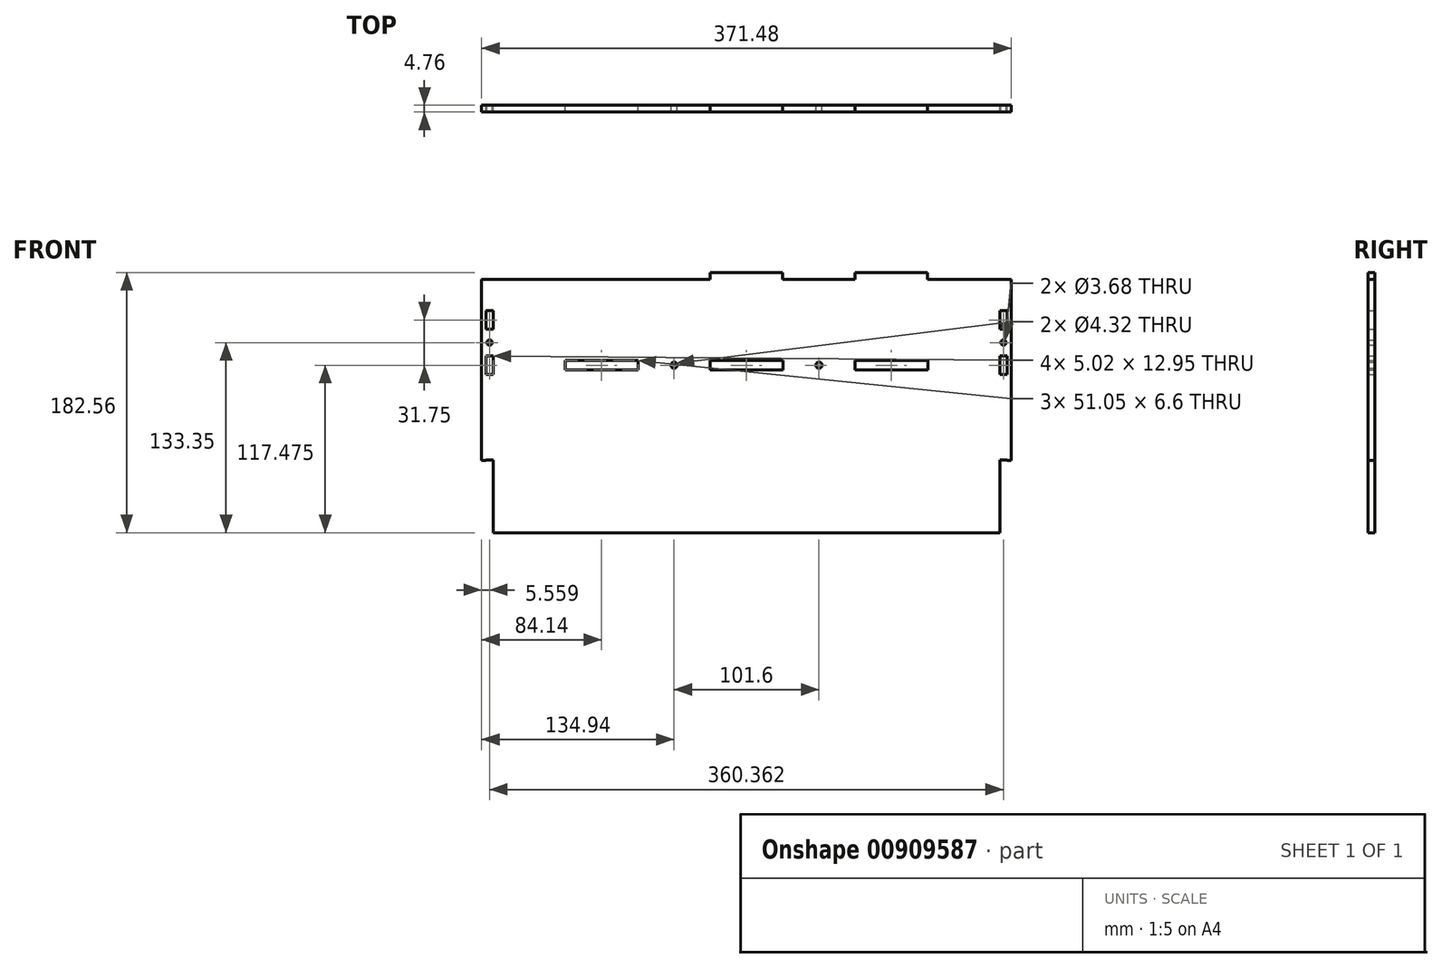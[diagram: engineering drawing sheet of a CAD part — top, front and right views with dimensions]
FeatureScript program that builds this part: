
annotation { "Feature Type Name" : "Feature", "Feature Type Description" : "" }
export const myFeature = defineFeature(function(context is Context, id is Id, definition is map)
    precondition{}
    {
        {
            var Q0;
            Q0=qCreatedBy(makeId("Front.planeOp"),FACE);
            var sketch = newSketch(context, id + "F0", { "sketchPlane" : qUnion([Q0])});
            skLineSegment(sketch, "E0.bottom", {"start": v(-182.56, 88.9) * mm, "end": v(182.56, 88.9) * mm});
            skLineSegment(sketch, "E0.top", {"start": v(-182.56, -88.9) * mm, "end": v(182.56, -88.9) * mm});
            skLineSegment(sketch, "E0.left", {"start": v(-182.56, 88.9) * mm, "end": v(-182.56, -88.9) * mm});
            skLineSegment(sketch, "E0.right", {"start": v(182.56, 88.9) * mm, "end": v(182.56, -88.9) * mm});
            skPoint(sketch, "E0.middle", {"position": v(0, 0) * mm});
            skLineSegment(sketch, "E1.0", {"start": v(-177.8, 88.9) * mm, "end": v(-177.8, -88.9) * mm, "construction": true});
            skLineSegment(sketch, "E2.0", {"start": v(177.8, 88.9) * mm, "end": v(177.8, -88.9) * mm, "construction": true});
            skLineSegment(sketch, "E3.bottom", {"start": v(-127, 31.75) * mm, "end": v(-76.2, 31.75) * mm});
            skLineSegment(sketch, "E3.top", {"start": v(-127, 25.4) * mm, "end": v(-76.2, 25.4) * mm});
            skLineSegment(sketch, "E3.left", {"start": v(-127, 31.75) * mm, "end": v(-127, 25.4) * mm});
            skLineSegment(sketch, "E3.right", {"start": v(-76.2, 31.75) * mm, "end": v(-76.2, 25.4) * mm});
            skLineSegment(sketch, "E4.0", {"start": v(-127.13, 31.88) * mm, "end": v(-76.07, 31.88) * mm});
            skLineSegment(sketch, "E4.1", {"start": v(-127.13, 31.88) * mm, "end": v(-127.13, 25.27) * mm});
            skLineSegment(sketch, "E4.2", {"start": v(-127.13, 25.27) * mm, "end": v(-76.07, 25.27) * mm});
            skLineSegment(sketch, "E4.3", {"start": v(-76.07, 31.88) * mm, "end": v(-76.07, 25.27) * mm});
            skLineSegment(sketch, "E5.1.0.0", {"start": v(-25.53, 31.88) * mm, "end": v(-25.53, 25.27) * mm});
            skLineSegment(sketch, "E5.1.0.1", {"start": v(-25.53, 31.88) * mm, "end": v(25.53, 31.88) * mm});
            skLineSegment(sketch, "E5.1.0.2", {"start": v(-25.53, 25.27) * mm, "end": v(25.53, 25.27) * mm});
            skLineSegment(sketch, "E5.1.0.3", {"start": v(25.4, 31.75) * mm, "end": v(25.4, 25.4) * mm});
            skLineSegment(sketch, "E5.1.0.4", {"start": v(-25.4, 31.75) * mm, "end": v(25.4, 31.75) * mm});
            skLineSegment(sketch, "E5.1.0.5", {"start": v(25.53, 31.88) * mm, "end": v(25.53, 25.27) * mm});
            skLineSegment(sketch, "E5.1.0.6", {"start": v(-25.4, 31.75) * mm, "end": v(-25.4, 25.4) * mm});
            skLineSegment(sketch, "E5.1.0.7", {"start": v(-25.4, 25.4) * mm, "end": v(25.4, 25.4) * mm});
            skLineSegment(sketch, "E5.2.0.0", {"start": v(76.07, 31.88) * mm, "end": v(76.07, 25.27) * mm});
            skLineSegment(sketch, "E5.2.0.1", {"start": v(76.07, 31.88) * mm, "end": v(127.13, 31.88) * mm});
            skLineSegment(sketch, "E5.2.0.2", {"start": v(76.07, 25.27) * mm, "end": v(127.13, 25.27) * mm});
            skLineSegment(sketch, "E5.2.0.3", {"start": v(127, 31.75) * mm, "end": v(127, 25.4) * mm});
            skLineSegment(sketch, "E5.2.0.4", {"start": v(76.2, 31.75) * mm, "end": v(127, 31.75) * mm});
            skLineSegment(sketch, "E5.2.0.5", {"start": v(127.13, 31.88) * mm, "end": v(127.13, 25.27) * mm});
            skLineSegment(sketch, "E5.2.0.6", {"start": v(76.2, 31.75) * mm, "end": v(76.2, 25.4) * mm});
            skLineSegment(sketch, "E5.2.0.7", {"start": v(76.2, 25.4) * mm, "end": v(127, 25.4) * mm});
            skLineSegment(sketch, "E5.direction1", {"start": v(-127, 25.4) * mm, "end": v(-25.4, 25.4) * mm, "construction": true});
            skLineSegment(sketch, "E6.bottom", {"start": v(-182.56, -88.9) * mm, "end": v(-177.8, -88.9) * mm});
            skLineSegment(sketch, "E6.top", {"start": v(-185.74, -38.1) * mm, "end": v(-177.8, -38.1) * mm});
            skLineSegment(sketch, "E6.left", {"start": v(-182.56, -88.9) * mm, "end": v(-182.56, -38.1) * mm});
            skLineSegment(sketch, "E6.right", {"start": v(-177.8, -88.9) * mm, "end": v(-177.8, -38.1) * mm});
            skLineSegment(sketch, "E7", {"start": v(0, 88.9) * mm, "end": v(0, -88.9) * mm, "construction": true});
            skLineSegment(sketch, "E8.MirrorCS", {"start": v(182.56, -88.9) * mm, "end": v(177.8, -88.9) * mm});
            skLineSegment(sketch, "E9.MirrorCS", {"start": v(182.56, -38.1) * mm, "end": v(177.8, -38.1) * mm});
            skLineSegment(sketch, "E10.MirrorCS", {"start": v(182.56, -88.9) * mm, "end": v(182.56, -38.1) * mm});
            skLineSegment(sketch, "E11.MirrorCS", {"start": v(177.8, -88.9) * mm, "end": v(177.8, -38.1) * mm});
            skLineSegment(sketch, "E12.0", {"start": v(-182.69, -89.03) * mm, "end": v(-177.67, -89.03) * mm});
            skLineSegment(sketch, "E12.1", {"start": v(-182.69, -89.03) * mm, "end": v(-182.69, -37.97) * mm});
            skLineSegment(sketch, "E12.2", {"start": v(-182.69, -37.97) * mm, "end": v(-177.67, -37.97) * mm});
            skLineSegment(sketch, "E12.3", {"start": v(-177.67, -89.03) * mm, "end": v(-177.67, -37.97) * mm});
            skLineSegment(sketch, "E13.bottom", {"start": v(-127, 88.9) * mm, "end": v(-76.2, 88.9) * mm});
            skLineSegment(sketch, "E13.top", {"start": v(-127, 93.66) * mm, "end": v(-76.2, 93.66) * mm});
            skLineSegment(sketch, "E13.left", {"start": v(-127, 88.9) * mm, "end": v(-127, 93.66) * mm});
            skLineSegment(sketch, "E13.right", {"start": v(-76.2, 88.9) * mm, "end": v(-76.2, 93.66) * mm});
            skLineSegment(sketch, "E14.1.0.0", {"start": v(-25.4, 93.66) * mm, "end": v(25.4, 93.66) * mm});
            skLineSegment(sketch, "E14.1.0.1", {"start": v(-25.4, 88.9) * mm, "end": v(25.4, 88.9) * mm});
            skLineSegment(sketch, "E14.1.0.2", {"start": v(-25.4, 88.9) * mm, "end": v(-25.4, 93.66) * mm});
            skLineSegment(sketch, "E14.1.0.3", {"start": v(25.4, 88.9) * mm, "end": v(25.4, 93.66) * mm});
            skLineSegment(sketch, "E14.2.0.0", {"start": v(76.2, 93.66) * mm, "end": v(127, 93.66) * mm});
            skLineSegment(sketch, "E14.2.0.1", {"start": v(76.2, 88.9) * mm, "end": v(127, 88.9) * mm});
            skLineSegment(sketch, "E14.2.0.2", {"start": v(76.2, 88.9) * mm, "end": v(76.2, 93.66) * mm});
            skLineSegment(sketch, "E14.2.0.3", {"start": v(127, 88.9) * mm, "end": v(127, 93.66) * mm});
            skLineSegment(sketch, "E14.direction1", {"start": v(-127, 88.9) * mm, "end": v(-25.4, 88.9) * mm, "construction": true});
            skLineSegment(sketch, "E15.MirrorCS", {"start": v(182.69, -89.03) * mm, "end": v(177.67, -89.03) * mm});
            skLineSegment(sketch, "E16.MirrorCS", {"start": v(182.69, -37.97) * mm, "end": v(177.67, -37.97) * mm});
            skLineSegment(sketch, "E17.MirrorCS", {"start": v(182.69, -89.03) * mm, "end": v(182.69, -37.97) * mm});
            skLineSegment(sketch, "E18.MirrorCS", {"start": v(177.67, -89.03) * mm, "end": v(177.67, -37.97) * mm});
            skCircle(sketch, "E19", {"center": v(-180.18, 44.45) * mm, "radius": 1.84 * mm});
            skCircle(sketch, "E20.MirrorC", {"center": v(180.18, 44.45) * mm, "radius": 1.84 * mm});
            skLineSegment(sketch, "E21.0", {"start": v(-185.74, 88.9) * mm, "end": v(-185.74, -38.1) * mm});
            skLineSegment(sketch, "E22", {"start": v(-185.74, 88.9) * mm, "end": v(-182.56, 88.9) * mm});
            skLineSegment(sketch, "E23.MirrorCS", {"start": v(185.74, -38.1) * mm, "end": v(177.8, -38.1) * mm});
            skLineSegment(sketch, "E24.MirrorCS", {"start": v(185.74, 88.9) * mm, "end": v(182.56, 88.9) * mm});
            skLineSegment(sketch, "E25.MirrorCS", {"start": v(185.74, 88.9) * mm, "end": v(185.74, -38.1) * mm});
            skLineSegment(sketch, "E26.bottom", {"start": v(-177.67, 35.05) * mm, "end": v(-182.69, 35.05) * mm});
            skLineSegment(sketch, "E26.top", {"start": v(-177.67, 22.1) * mm, "end": v(-182.69, 22.1) * mm});
            skLineSegment(sketch, "E26.left", {"start": v(-177.67, 35.05) * mm, "end": v(-177.67, 22.1) * mm});
            skLineSegment(sketch, "E26.right", {"start": v(-182.69, 35.05) * mm, "end": v(-182.69, 22.1) * mm});
            skPoint(sketch, "E26.middle", {"position": v(-180.18, 28.58) * mm});
            skPoint(sketch, "E26.middle.positionSnap0", {"position": v(-180.18, -37.97) * mm});
            skPoint(sketch, "E26.centerSnap0", {"position": v(-180.18, -37.97) * mm});
            skLineSegment(sketch, "E27", {"start": v(-185.74, 44.45) * mm, "end": v(-177.8, 44.45) * mm, "construction": true});
            skLineSegment(sketch, "E28.MirrorCS", {"start": v(-177.67, 53.85) * mm, "end": v(-182.69, 53.85) * mm});
            skPoint(sketch, "E29.MirrorP", {"position": v(-180.18, 60.33) * mm});
            skLineSegment(sketch, "E30.MirrorCS", {"start": v(-177.67, 66.8) * mm, "end": v(-182.69, 66.8) * mm});
            skLineSegment(sketch, "E31.MirrorCS", {"start": v(-182.69, 53.85) * mm, "end": v(-182.69, 66.8) * mm});
            skLineSegment(sketch, "E32.MirrorCS", {"start": v(-177.67, 53.85) * mm, "end": v(-177.67, 66.8) * mm});
            skLineSegment(sketch, "E33.MirrorCS", {"start": v(182.69, 53.85) * mm, "end": v(182.69, 66.8) * mm});
            skLineSegment(sketch, "E34.MirrorCS", {"start": v(177.67, 66.8) * mm, "end": v(182.69, 66.8) * mm});
            skLineSegment(sketch, "E35.MirrorCS", {"start": v(177.67, 53.85) * mm, "end": v(177.67, 66.8) * mm});
            skLineSegment(sketch, "E36.MirrorCS", {"start": v(177.67, 53.85) * mm, "end": v(182.69, 53.85) * mm});
            skPoint(sketch, "E37.MirrorP", {"position": v(180.18, 60.33) * mm});
            skLineSegment(sketch, "E38.MirrorCS", {"start": v(177.67, 35.05) * mm, "end": v(182.69, 35.05) * mm});
            skLineSegment(sketch, "E39.MirrorCS", {"start": v(182.69, 35.05) * mm, "end": v(182.69, 22.1) * mm});
            skLineSegment(sketch, "E40.MirrorCS", {"start": v(177.67, 35.05) * mm, "end": v(177.67, 22.1) * mm});
            skLineSegment(sketch, "E41.MirrorCS", {"start": v(177.67, 22.1) * mm, "end": v(182.69, 22.1) * mm});
            skPoint(sketch, "E42.MirrorP", {"position": v(180.18, 28.57) * mm});
            skLineSegment(sketch, "E43", {"start": v(-127, 28.58) * mm, "end": v(-177.8, 28.58) * mm, "construction": true});
            skPoint(sketch, "E43.endSnap0", {"position": v(-177.67, 28.58) * mm});
            skLineSegment(sketch, "E44", {"start": v(-76.2, 28.58) * mm, "end": v(-25.4, 28.58) * mm, "construction": true});
            skLineSegment(sketch, "E45", {"start": v(25.4, 28.58) * mm, "end": v(76.2, 28.58) * mm, "construction": true});
            skLineSegment(sketch, "E46", {"start": v(127, 28.58) * mm, "end": v(177.8, 28.58) * mm, "construction": true});
            skCircle(sketch, "E47", {"center": v(-152.4, 28.58) * mm, "radius": 1.59 * mm, "construction": true});
            skCircle(sketch, "E48", {"center": v(-50.8, 28.58) * mm, "radius": 1.59 * mm, "construction": true});
            skCircle(sketch, "E49", {"center": v(50.8, 28.58) * mm, "radius": 1.59 * mm, "construction": true});
            skCircle(sketch, "E50", {"center": v(152.4, 28.58) * mm, "radius": 1.59 * mm, "construction": true});
            skSolve(sketch);
        }
        {
            var Q0;
            Q0=makeQuery(id+"F0.imprint","IMPRINT",FACE,{"disambiguationData":[TD([[makeQuery(id+"F0.imprint","IMPRINT",EDGE,{"derivedFrom":sQuery(id+"F0.wireOp",EDGE,"E0.bottom")}),-1.0]])]});
            var Q1;
            Q1=makeQuery(id+"F0.imprint","IMPRINT",FACE,{"disambiguationData":[TD([[makeQuery(id+"F0.imprint","IMPRINT",EDGE,{"derivedFrom":sQuery(id+"F0.wireOp",EDGE,"E13.bottom")}),1.0]])]});
            var Q2;
            Q2=makeQuery(id+"F0.imprint","IMPRINT",FACE,{"disambiguationData":[TD([[makeQuery(id+"F0.imprint","IMPRINT",EDGE,{"derivedFrom":sQuery(id+"F0.wireOp",EDGE,"E14.1.0.0")}),-1.0]])]});
            var Q3;
            Q3=makeQuery(id+"F0.imprint","IMPRINT",FACE,{"disambiguationData":[TD([[makeQuery(id+"F0.imprint","IMPRINT",EDGE,{"derivedFrom":sQuery(id+"F0.wireOp",EDGE,"E14.2.0.0")}),-1.0]])]});
            var Q4;
            {var subQ9=sQuery(id+"F0.wireOp",EDGE,"E22");Q4=makeQuery(id+"F0.imprint","IMPRINT",FACE,{"disambiguationData":[TD([[makeQuery(id+"F0.imprint","IMPRINT",EDGE,{"derivedFrom":subQ9}),-1.0]])]});}
            var Q5;
            {var subQ6=sQuery(id+"F0.wireOp",EDGE,"E24.MirrorCS");Q5=makeQuery(id+"F0.imprint","IMPRINT",FACE,{"disambiguationData":[TD([[makeQuery(id+"F0.imprint","IMPRINT",EDGE,{"derivedFrom":subQ6}),1.0]])]});}
            extrude(context, id + "F1", {"entities" : qUnion([Q0, Q1, Q2, Q3, Q4, Q5]), "depth" : 4.76 * mm, "offsetDistance" : 25.4 * mm});
        }
        {
            var Q0;
            Q0=sQuery(id+"F0.wireOp",VERTEX,"E48.center");
            var Q1;
            Q1=sQuery(id+"F0.wireOp",VERTEX,"E49.center");
            var Q2;
            Q2=makeQuery(id+"F1.opExtrude","SWEPT_BODY",BODY,{"disambiguationData":[OSD([sQuery(id+"F0.wireOp",EDGE,"E0.bottom"),sQuery(id+"F0.wireOp",EDGE,"E0.top"),sQuery(id+"F0.wireOp",EDGE,"E4.0"),sQuery(id+"F0.wireOp",EDGE,"E4.1"),sQuery(id+"F0.wireOp",EDGE,"E4.2"),sQuery(id+"F0.wireOp",EDGE,"E4.3"),sQuery(id+"F0.wireOp",EDGE,"E5.1.0.0"),sQuery(id+"F0.wireOp",EDGE,"E5.1.0.1"),sQuery(id+"F0.wireOp",EDGE,"E5.1.0.2"),sQuery(id+"F0.wireOp",EDGE,"E5.1.0.5"),sQuery(id+"F0.wireOp",EDGE,"E5.2.0.0"),sQuery(id+"F0.wireOp",EDGE,"E5.2.0.1"),sQuery(id+"F0.wireOp",EDGE,"E5.2.0.2"),sQuery(id+"F0.wireOp",EDGE,"E5.2.0.5"),sQuery(id+"F0.wireOp",EDGE,"E6.top"),sQuery(id+"F0.wireOp",EDGE,"E12.1"),sQuery(id+"F0.wireOp",EDGE,"E12.2"),sQuery(id+"F0.wireOp",EDGE,"E12.3"),sQuery(id+"F0.wireOp",EDGE,"E13.top"),sQuery(id+"F0.wireOp",EDGE,"E13.left"),sQuery(id+"F0.wireOp",EDGE,"E13.right"),sQuery(id+"F0.wireOp",EDGE,"E14.1.0.0"),sQuery(id+"F0.wireOp",EDGE,"E14.1.0.2"),sQuery(id+"F0.wireOp",EDGE,"E14.1.0.3"),sQuery(id+"F0.wireOp",EDGE,"E14.2.0.0"),sQuery(id+"F0.wireOp",EDGE,"E14.2.0.2"),sQuery(id+"F0.wireOp",EDGE,"E14.2.0.3"),sQuery(id+"F0.wireOp",EDGE,"E17.MirrorCS"),sQuery(id+"F0.wireOp",EDGE,"E18.MirrorCS"),sQuery(id+"F0.wireOp",EDGE,"E19"),sQuery(id+"F0.wireOp",EDGE,"E21.0"),sQuery(id+"F0.wireOp",EDGE,"E22"),sQuery(id+"F0.wireOp",EDGE,"E23.MirrorCS"),sQuery(id+"F0.wireOp",EDGE,"E24.MirrorCS"),sQuery(id+"F0.wireOp",EDGE,"E16.MirrorCS"),sQuery(id+"F0.wireOp",EDGE,"E20.MirrorC"),sQuery(id+"F0.wireOp",EDGE,"E25.MirrorCS"),sQuery(id+"F0.wireOp",EDGE,"E26.bottom"),sQuery(id+"F0.wireOp",EDGE,"E26.top"),sQuery(id+"F0.wireOp",EDGE,"E26.left"),sQuery(id+"F0.wireOp",EDGE,"E26.right"),sQuery(id+"F0.wireOp",EDGE,"E28.MirrorCS"),sQuery(id+"F0.wireOp",EDGE,"E30.MirrorCS"),sQuery(id+"F0.wireOp",EDGE,"E31.MirrorCS"),sQuery(id+"F0.wireOp",EDGE,"E32.MirrorCS"),sQuery(id+"F0.wireOp",EDGE,"E33.MirrorCS"),sQuery(id+"F0.wireOp",EDGE,"E34.MirrorCS"),sQuery(id+"F0.wireOp",EDGE,"E35.MirrorCS"),sQuery(id+"F0.wireOp",EDGE,"E36.MirrorCS"),sQuery(id+"F0.wireOp",EDGE,"E38.MirrorCS"),sQuery(id+"F0.wireOp",EDGE,"E39.MirrorCS"),sQuery(id+"F0.wireOp",EDGE,"E40.MirrorCS"),sQuery(id+"F0.wireOp",EDGE,"E41.MirrorCS")])]});
            hole(context, id + "F2", {"style" : HoleStyle.SIMPLE, "endStyle" : HoleEndStyle.BLIND, "oppositeDirection" : true, "standardTappedOrClearance" : lookupTablePath({ "fit" : "Normal (ASME)", "standard" : "ANSI", "size" : "#6", "type" : "Clearance" }), "standardBlindInLast" : lookupTablePath({ "fit" : "Normal", "standard" : "ANSI", "size" : "#6", "type" : "Clearance" }), "holeDiameter" : 4.32 * mm, "majorDiameter" : 6.35 * mm, "holeDepth" : 11.9 * mm, "isTappedThrough" : true, "tappedDepth" : 9.52 * mm, "tapClearance" : 3, "locations" : qUnion([Q0, Q1]), "scope" : qUnion([Q2])});
        }
    });
